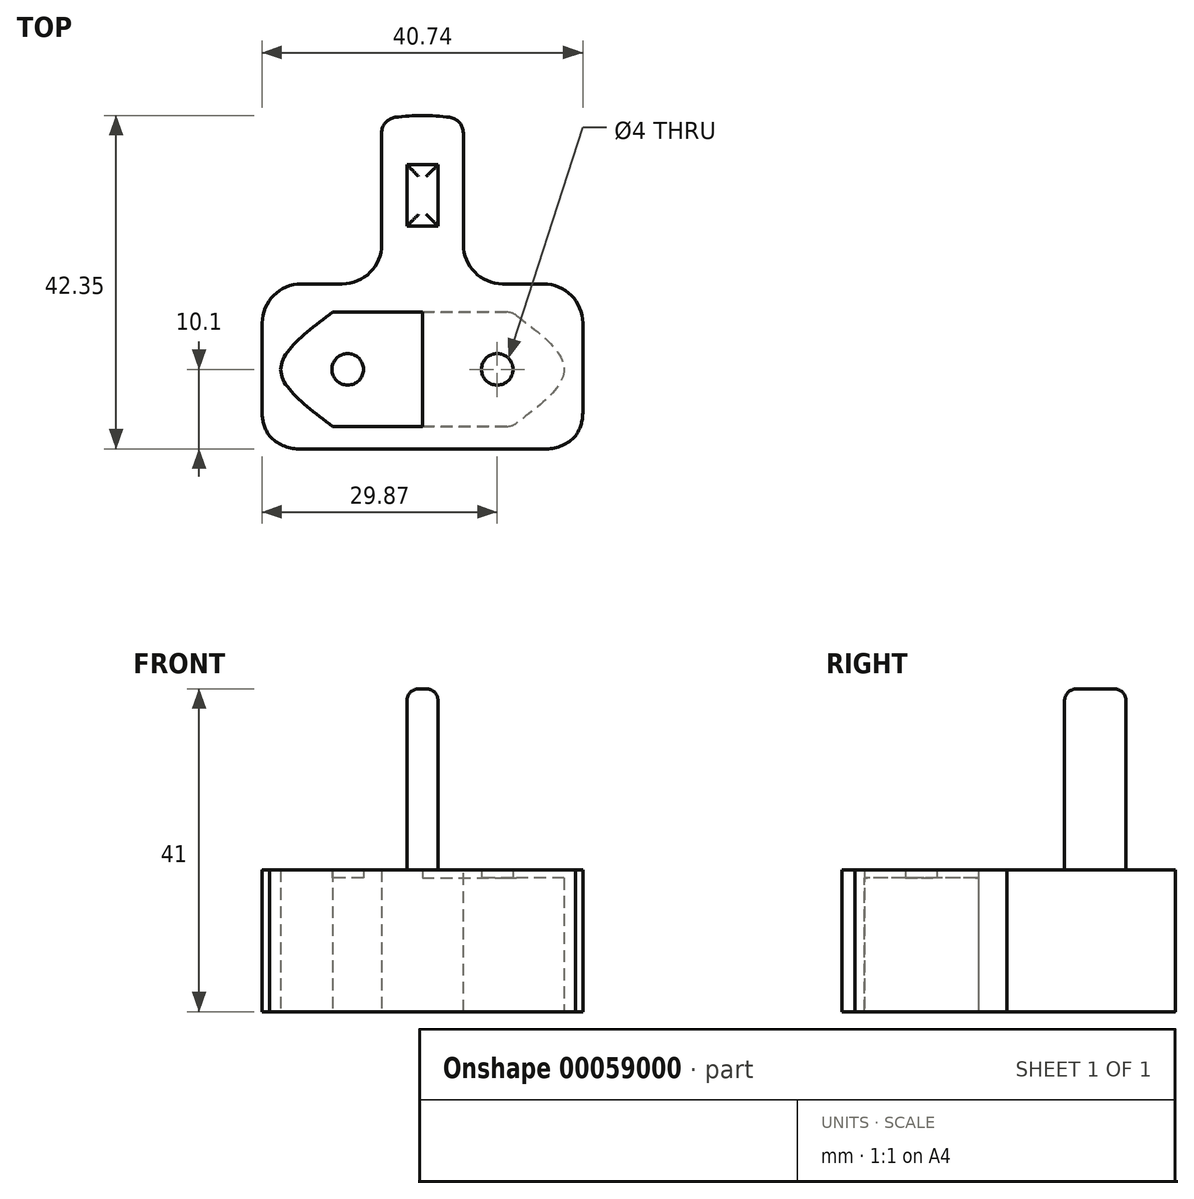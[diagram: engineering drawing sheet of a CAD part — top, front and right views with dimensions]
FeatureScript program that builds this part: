
annotation { "Feature Type Name" : "Feature", "Feature Type Description" : "" }
export const myFeature = defineFeature(function(context is Context, id is Id, definition is map)
    precondition{}
    {
        {
            var Q0;
            Q0=qCreatedBy(makeId("Top.planeOp"),FACE);
            var sketch = newSketch(context, id + "F0", { "sketchPlane" : qUnion([Q0])});
            skArc(sketch, "E0", {"start": v(-20.37, -14.5) * mm, "mid": v(-19.24, -15.97) * mm, "end": v(-18, -17.35) * mm});
            skLineSegment(sketch, "E1.bottom", {"start": v(0, 0) * mm, "end": v(18, 0) * mm});
            skLineSegment(sketch, "E1.top", {"start": v(0, -14.5) * mm, "end": v(18, -14.5) * mm});
            skLineSegment(sketch, "E1.left", {"start": v(0, 0) * mm, "end": v(0, -14.5) * mm});
            skLineSegment(sketch, "E1.right", {"start": v(18, 0) * mm, "end": v(18, -14.5) * mm});
            skLineSegment(sketch, "E2.bottom", {"start": v(0, 10.95) * mm, "end": v(1.98, 10.95) * mm});
            skLineSegment(sketch, "E2.top", {"start": v(0, 18.75) * mm, "end": v(1.98, 18.75) * mm});
            skLineSegment(sketch, "E2.left", {"start": v(0, 10.95) * mm, "end": v(0, 18.75) * mm});
            skLineSegment(sketch, "E2.right", {"start": v(1.98, 10.95) * mm, "end": v(1.98, 18.75) * mm});
            skLineSegment(sketch, "E3", {"start": v(18, -7.25) * mm, "end": v(0, -7.25) * mm});
            skCircle(sketch, "E4", {"center": v(9.5, -7.25) * mm, "radius": 2 * mm});
            skLineSegment(sketch, "E5", {"start": v(11.4, 0) * mm, "end": v(11.4, -14.5) * mm, "construction": true});
            skFitSpline(sketch, "E6", {"points": [v(11.4, 0) * mm, v(18, -7.25) * mm, v(11.4, -14.5) * mm], "startDerivative": vector(19.06, -14.35) * mm, "endDerivative": vector(-19.06, -14.35) * mm});
            skLineSegment(sketch, "E7", {"start": v(0, 25) * mm, "end": v(0, -25) * mm, "construction": true});
            skLineSegment(sketch, "E8.MirrorCS", {"start": v(0, 10.95) * mm, "end": v(-1.98, 10.95) * mm});
            skLineSegment(sketch, "E9.MirrorCS", {"start": v(0, 18.75) * mm, "end": v(-1.98, 18.75) * mm});
            skLineSegment(sketch, "E10.MirrorCS", {"start": v(-1.98, 10.95) * mm, "end": v(-1.98, 18.75) * mm});
            skLineSegment(sketch, "E11.MirrorCS", {"start": v(-11.4, 0) * mm, "end": v(-11.4, -14.5) * mm, "construction": true});
            skLineSegment(sketch, "E12.MirrorCS", {"start": v(-18, 0) * mm, "end": v(-18, -14.5) * mm});
            skFitSpline(sketch, "E13.MirrorCS", {"points": [v(-11.4, 0) * mm, v(-18, -7.25) * mm, v(-11.4, -14.5) * mm], "startDerivative": vector(-19.06, -14.35) * mm, "endDerivative": vector(19.06, -14.35) * mm});
            skCircle(sketch, "E14.MirrorC", {"center": v(-9.5, -7.25) * mm, "radius": 2 * mm});
            skLineSegment(sketch, "E15.MirrorCS", {"start": v(-18, -7.25) * mm, "end": v(0, -7.25) * mm});
            skLineSegment(sketch, "E16.MirrorCS", {"start": v(0, 0) * mm, "end": v(-18, 0) * mm});
            skLineSegment(sketch, "E17.MirrorCS", {"start": v(0, -14.5) * mm, "end": v(-18, -14.5) * mm});
            skLineSegment(sketch, "E18", {"start": v(-18, -17.35) * mm, "end": v(18, -17.35) * mm});
            skLineSegment(sketch, "E19", {"start": v(-20.37, -14.5) * mm, "end": v(-20.37, 14.5) * mm});
            skLineSegment(sketch, "E20", {"start": v(20.37, -14.5) * mm, "end": v(20.37, 14.5) * mm});
            skArc(sketch, "E21.trimOffspring", {"start": v(5.19, 24.46) * mm, "mid": v(0, 25) * mm, "end": v(-5.19, 24.46) * mm});
            skArc(sketch, "E22.trimOffspring", {"start": v(18, -17.35) * mm, "mid": v(19.24, -15.97) * mm, "end": v(20.37, -14.5) * mm});
            skLineSegment(sketch, "E23", {"start": v(-5.19, 24.46) * mm, "end": v(-5.19, 3.6) * mm});
            skLineSegment(sketch, "E24", {"start": v(-5.19, 3.6) * mm, "end": v(-20.37, 3.6) * mm});
            skLineSegment(sketch, "E25", {"start": v(5.19, 24.46) * mm, "end": v(5.19, 3.6) * mm});
            skLineSegment(sketch, "E26", {"start": v(5.19, 3.6) * mm, "end": v(20.37, 3.6) * mm});
            skLineSegment(sketch, "E27", {"start": v(11.4, 0) * mm, "end": v(18, -7.25) * mm, "construction": true});
            skLineSegment(sketch, "E28", {"start": v(11.4, -14.5) * mm, "end": v(18, -7.25) * mm, "construction": true});
            skLineSegment(sketch, "E29", {"start": v(-11.4, 0) * mm, "end": v(-18, -7.25) * mm, "construction": true});
            skLineSegment(sketch, "E30", {"start": v(-18, -7.25) * mm, "end": v(-11.4, -14.5) * mm, "construction": true});
            skLineSegment(sketch, "E31", {"start": v(-18, -14.5) * mm, "end": v(18, 0) * mm, "construction": true});
            skLineSegment(sketch, "E32", {"start": v(-18, 0) * mm, "end": v(18, -14.5) * mm, "construction": true});
            skSolve(sketch);
        }
        {
            var Q0;
            Q0 = qSketchRegion(id + "F0", true);
            var Q1;
            Q1=makeQuery(id+"F0.imprint","IMPRINT",FACE,{"disambiguationData":[TD([[makeQuery(id+"F0.imprint","IMPRINT",EDGE,{"derivedFrom":sQuery(id+"F0.wireOp",EDGE,"E2.left")}),1.0]])]});
            var Q2;
            Q2=makeQuery(id+"F0.imprint","IMPRINT",FACE,{"disambiguationData":[TD([[makeQuery(id+"F0.imprint","IMPRINT",EDGE,{"derivedFrom":sQuery(id+"F0.wireOp",EDGE,"E2.bottom")}),1.0]])]});
            var Q3;
            {var subQ0=sQuery(id+"F0.wireOp",EDGE,"E16.MirrorCS");var subQ1=sQuery(id+"F0.wireOp",EDGE,"E12.MirrorCS");var subQ2=makeQuery(id+"F0.imprint","INTERSECT",VERTEX,{"derivedFrom":[subQ1,subQ0]});Q3=makeQuery(id+"F0.imprint","IMPRINT",FACE,{"disambiguationData":[TD([[makeQuery(id+"F0.imprint","IMPRINT",EDGE,{"disambiguationData":[TD([[subQ2,1.0]])],"derivedFrom":subQ0}),1.0]])]});}
            var Q4;
            {var subQ0=sQuery(id+"F0.wireOp",EDGE,"E1.right");var subQ1=sQuery(id+"F0.wireOp",EDGE,"E1.bottom");var subQ2=makeQuery(id+"F0.imprint","INTERSECT",VERTEX,{"derivedFrom":[subQ1,subQ0]});Q4=makeQuery(id+"F0.imprint","IMPRINT",FACE,{"disambiguationData":[TD([[makeQuery(id+"F0.imprint","IMPRINT",EDGE,{"disambiguationData":[TD([[subQ2,1.0]])],"derivedFrom":subQ1}),-1.0]])]});}
            var Q5;
            {var subQ0=sQuery(id+"F0.wireOp",EDGE,"E1.right");var subQ1=sQuery(id+"F0.wireOp",EDGE,"E1.top");var subQ2=makeQuery(id+"F0.imprint","INTERSECT",VERTEX,{"derivedFrom":[subQ1,subQ0]});Q5=makeQuery(id+"F0.imprint","IMPRINT",FACE,{"disambiguationData":[TD([[makeQuery(id+"F0.imprint","IMPRINT",EDGE,{"disambiguationData":[TD([[subQ2,1.0]])],"derivedFrom":subQ1}),1.0]])]});}
            var Q6;
            {var subQ0=sQuery(id+"F0.wireOp",EDGE,"E17.MirrorCS");var subQ1=sQuery(id+"F0.wireOp",EDGE,"E12.MirrorCS");var subQ2=makeQuery(id+"F0.imprint","INTERSECT",VERTEX,{"derivedFrom":[subQ1,subQ0]});Q6=makeQuery(id+"F0.imprint","IMPRINT",FACE,{"disambiguationData":[TD([[makeQuery(id+"F0.imprint","IMPRINT",EDGE,{"disambiguationData":[TD([[subQ2,1.0]])],"derivedFrom":subQ0}),-1.0]])]});}
            var Q7;
            {var subQ0=sQuery(id+"F0.wireOp",EDGE,"E15.MirrorCS");var subQ3=sQuery(id+"F0.wireOp",EDGE,"E14.MirrorC");var subQ4=makeQuery(id+"F0.imprint","INTERSECT",VERTEX,{"disambiguationData":[OD(0.0)],"derivedFrom":[subQ3,subQ0]});Q7=makeQuery(id+"F0.imprint","IMPRINT",FACE,{"disambiguationData":[TD([[makeQuery(id+"F0.imprint","IMPRINT",EDGE,{"disambiguationData":[TD([[subQ4,-1.0]])],"derivedFrom":subQ3}),1.0]])]});}
            var Q8;
            {var subQ0=sQuery(id+"F0.wireOp",EDGE,"E3");var subQ3=sQuery(id+"F0.wireOp",EDGE,"E4");var subQ7=makeQuery(id+"F0.imprint","INTERSECT",VERTEX,{"disambiguationData":[OD(0.0)],"derivedFrom":[subQ0,subQ3]});Q8=makeQuery(id+"F0.imprint","IMPRINT",FACE,{"disambiguationData":[TD([[makeQuery(id+"F0.imprint","IMPRINT",EDGE,{"disambiguationData":[TD([[subQ7,-1.0]])],"derivedFrom":subQ3}),-1.0]])]});}
            var Q9;
            {var subQ0=sQuery(id+"F0.wireOp",EDGE,"E15.MirrorCS");var subQ3=sQuery(id+"F0.wireOp",EDGE,"E14.MirrorC");var subQ4=makeQuery(id+"F0.imprint","INTERSECT",VERTEX,{"disambiguationData":[OD(0.0)],"derivedFrom":[subQ3,subQ0]});Q9=makeQuery(id+"F0.imprint","IMPRINT",FACE,{"disambiguationData":[TD([[makeQuery(id+"F0.imprint","IMPRINT",EDGE,{"disambiguationData":[TD([[subQ4,1.0]])],"derivedFrom":subQ3}),1.0]])]});}
            var Q10;
            {var subQ0=sQuery(id+"F0.wireOp",EDGE,"E3");var subQ3=sQuery(id+"F0.wireOp",EDGE,"E4");var subQ7=makeQuery(id+"F0.imprint","INTERSECT",VERTEX,{"disambiguationData":[OD(0.0)],"derivedFrom":[subQ0,subQ3]});Q10=makeQuery(id+"F0.imprint","IMPRINT",FACE,{"disambiguationData":[TD([[makeQuery(id+"F0.imprint","IMPRINT",EDGE,{"disambiguationData":[TD([[subQ7,1.0]])],"derivedFrom":subQ3}),-1.0]])]});}
            extrude(context, id + "F1", {"entities" : qUnion([Q0, Q1, Q2, Q3, Q4, Q5, Q6, Q7, Q8, Q9, Q10]), "depth" : 18 * mm});
        }
        {
            var Q0;
            Q0=makeQuery(id+"F0.imprint","IMPRINT",FACE,{"disambiguationData":[TD([[makeQuery(id+"F0.imprint","IMPRINT",EDGE,{"derivedFrom":sQuery(id+"F0.wireOp",EDGE,"E2.left")}),1.0]])]});
            var Q1;
            Q1=makeQuery(id+"F0.imprint","IMPRINT",FACE,{"disambiguationData":[TD([[makeQuery(id+"F0.imprint","IMPRINT",EDGE,{"derivedFrom":sQuery(id+"F0.wireOp",EDGE,"E2.bottom")}),1.0]])]});
            extrude(context, id + "F2", {"entities" : qUnion([Q0, Q1]), "operationType" : NewBodyOperationType.ADD, "depth" : 41 * mm});
        }
        {
            var Q0;
            {var subQ0=sQuery(id+"F0.wireOp",EDGE,"E15.MirrorCS");var subQ3=sQuery(id+"F0.wireOp",EDGE,"E14.MirrorC");var subQ4=makeQuery(id+"F0.imprint","INTERSECT",VERTEX,{"disambiguationData":[OD(0.0)],"derivedFrom":[subQ3,subQ0]});Q0=makeQuery(id+"F0.imprint","IMPRINT",FACE,{"disambiguationData":[TD([[makeQuery(id+"F0.imprint","IMPRINT",EDGE,{"disambiguationData":[TD([[subQ4,-1.0]])],"derivedFrom":subQ3}),1.0]])]});}
            var Q1;
            {var subQ0=sQuery(id+"F0.wireOp",EDGE,"E15.MirrorCS");var subQ3=sQuery(id+"F0.wireOp",EDGE,"E14.MirrorC");var subQ4=makeQuery(id+"F0.imprint","INTERSECT",VERTEX,{"disambiguationData":[OD(0.0)],"derivedFrom":[subQ3,subQ0]});Q1=makeQuery(id+"F0.imprint","IMPRINT",FACE,{"disambiguationData":[TD([[makeQuery(id+"F0.imprint","IMPRINT",EDGE,{"disambiguationData":[TD([[subQ4,1.0]])],"derivedFrom":subQ3}),1.0]])]});}
            var Q2;
            {var subQ0=sQuery(id+"F0.wireOp",EDGE,"E3");var subQ3=sQuery(id+"F0.wireOp",EDGE,"E4");var subQ7=makeQuery(id+"F0.imprint","INTERSECT",VERTEX,{"disambiguationData":[OD(0.0)],"derivedFrom":[subQ0,subQ3]});Q2=makeQuery(id+"F0.imprint","IMPRINT",FACE,{"disambiguationData":[TD([[makeQuery(id+"F0.imprint","IMPRINT",EDGE,{"disambiguationData":[TD([[subQ7,-1.0]])],"derivedFrom":subQ3}),-1.0]])]});}
            var Q3;
            {var subQ0=sQuery(id+"F0.wireOp",EDGE,"E3");var subQ3=sQuery(id+"F0.wireOp",EDGE,"E4");var subQ7=makeQuery(id+"F0.imprint","INTERSECT",VERTEX,{"disambiguationData":[OD(0.0)],"derivedFrom":[subQ0,subQ3]});Q3=makeQuery(id+"F0.imprint","IMPRINT",FACE,{"disambiguationData":[TD([[makeQuery(id+"F0.imprint","IMPRINT",EDGE,{"disambiguationData":[TD([[subQ7,1.0]])],"derivedFrom":subQ3}),-1.0]])]});}
            extrude(context, id + "F3", {"entities" : qUnion([Q0, Q1, Q2, Q3]), "operationType" : NewBodyOperationType.REMOVE, "depth" : 17 * mm});
        }
        {
            var Q0;
            Q0=makeQuery(id+"F2.opExtrude","CAP_FACE",FACE,{"disambiguationData":[OSD([sQuery(id+"F0.wireOp",EDGE,"E2.bottom"),sQuery(id+"F0.wireOp",EDGE,"E2.top"),sQuery(id+"F0.wireOp",EDGE,"E2.right"),sQuery(id+"F0.wireOp",EDGE,"E8.MirrorCS"),sQuery(id+"F0.wireOp",EDGE,"E9.MirrorCS"),sQuery(id+"F0.wireOp",EDGE,"E10.MirrorCS")])],"isStart":false});
            fillet(context, id + "F4", {"entities" : qUnion([Q0]), "radius" : 1.5 * mm, "tangentPropagation" : true, "allowEdgeOverflow" : false});
        }
        {
            var Q0;
            Q0=makeQuery(id+"F1.opExtrude","SWEPT_EDGE",EDGE,{"disambiguationData":[OSD([sQuery(id+"F0.wireOp",EDGE,"E19"),sQuery(id+"F0.wireOp",EDGE,"E24")])]});
            var Q1;
            Q1=makeQuery(id+"F1.opExtrude","SWEPT_EDGE",EDGE,{"disambiguationData":[OSD([sQuery(id+"F0.wireOp",EDGE,"E20"),sQuery(id+"F0.wireOp",EDGE,"E26")])]});
            var Q2;
            Q2=makeQuery(id+"F1.opExtrude","SWEPT_EDGE",EDGE,{"disambiguationData":[OSD([sQuery(id+"F0.wireOp",EDGE,"E25"),sQuery(id+"F0.wireOp",EDGE,"E26")])]});
            var Q3;
            Q3=makeQuery(id+"F1.opExtrude","SWEPT_EDGE",EDGE,{"disambiguationData":[OSD([sQuery(id+"F0.wireOp",EDGE,"E23"),sQuery(id+"F0.wireOp",EDGE,"E24")])]});
            var Q4;
            Q4=makeQuery(id+"F1.opExtrude","SWEPT_EDGE",EDGE,{"disambiguationData":[OSD([sQuery(id+"F0.wireOp",EDGE,"E0"),sQuery(id+"F0.wireOp",EDGE,"E18")])]});
            var Q5;
            Q5=makeQuery(id+"F1.opExtrude","SWEPT_EDGE",EDGE,{"disambiguationData":[OSD([sQuery(id+"F0.wireOp",EDGE,"E0"),sQuery(id+"F0.wireOp",EDGE,"E19")])]});
            var Q6;
            Q6=makeQuery(id+"F1.opExtrude","SWEPT_EDGE",EDGE,{"disambiguationData":[OSD([sQuery(id+"F0.wireOp",EDGE,"E18"),sQuery(id+"F0.wireOp",EDGE,"E22.trimOffspring")])]});
            var Q7;
            Q7=makeQuery(id+"F1.opExtrude","SWEPT_EDGE",EDGE,{"disambiguationData":[OSD([sQuery(id+"F0.wireOp",EDGE,"E20"),sQuery(id+"F0.wireOp",EDGE,"E22.trimOffspring")])]});
            fillet(context, id + "F5", {"entities" : qUnion([Q0, Q1, Q2, Q3, Q4, Q5, Q6, Q7]), "radius" : 5 * mm, "tangentPropagation" : true, "allowEdgeOverflow" : false});
        }
        {
            var Q0;
            Q0=makeQuery(id+"F1.opExtrude","SWEPT_EDGE",EDGE,{"disambiguationData":[OSD([sQuery(id+"F0.wireOp",EDGE,"E21.trimOffspring"),sQuery(id+"F0.wireOp",EDGE,"E25")])]});
            var Q1;
            Q1=makeQuery(id+"F1.opExtrude","SWEPT_EDGE",EDGE,{"disambiguationData":[OSD([sQuery(id+"F0.wireOp",EDGE,"E21.trimOffspring"),sQuery(id+"F0.wireOp",EDGE,"E23")])]});
            fillet(context, id + "F6", {"entities" : qUnion([Q0, Q1]), "radius" : 2 * mm, "tangentPropagation" : true, "allowEdgeOverflow" : false});
        }
        {
            var Q0;
            Q0=makeQuery(id+"F3.boolean.opBoolean","COPY",EDGE,{"derivedFrom":makeQuery(id+"F3.opExtrude","SWEPT_EDGE",EDGE,{"disambiguationData":[OSD([sQuery(id+"F0.wireOp",EDGE,"E1.bottom"),sQuery(id+"F0.wireOp",EDGE,"E6")])]})});
            var Q1;
            Q1=makeQuery(id+"F3.boolean.opBoolean","COPY",EDGE,{"derivedFrom":makeQuery(id+"F3.opExtrude","SWEPT_EDGE",EDGE,{"disambiguationData":[OSD([sQuery(id+"F0.wireOp",EDGE,"E1.top"),sQuery(id+"F0.wireOp",EDGE,"E6")])]})});
            var Q2;
            Q2=makeQuery(id+"F3.boolean.opBoolean","COPY",EDGE,{"derivedFrom":makeQuery(id+"F3.opExtrude","SWEPT_EDGE",EDGE,{"disambiguationData":[OSD([sQuery(id+"F0.wireOp",EDGE,"E13.MirrorCS"),sQuery(id+"F0.wireOp",EDGE,"E16.MirrorCS")])]})});
            var Q3;
            Q3=makeQuery(id+"F3.boolean.opBoolean","COPY",EDGE,{"derivedFrom":makeQuery(id+"F3.opExtrude","SWEPT_EDGE",EDGE,{"disambiguationData":[OSD([sQuery(id+"F0.wireOp",EDGE,"E13.MirrorCS"),sQuery(id+"F0.wireOp",EDGE,"E17.MirrorCS")])]})});
            var Q4;
            Q4=makeQuery(id+"F3.boolean.opBoolean","COPY",EDGE,{"derivedFrom":makeQuery(id+"F3.opExtrude","CAP_EDGE",EDGE,{"disambiguationData":[OSD([sQuery(id+"F0.wireOp",EDGE,"E6")])],"isStart":true})});
            fillet(context, id + "F7", {"entities" : qUnion([Q0, Q1, Q2, Q3, Q4]), "radius" : 2 * mm, "tangentPropagation" : true, "allowEdgeOverflow" : false});
        }
    });
